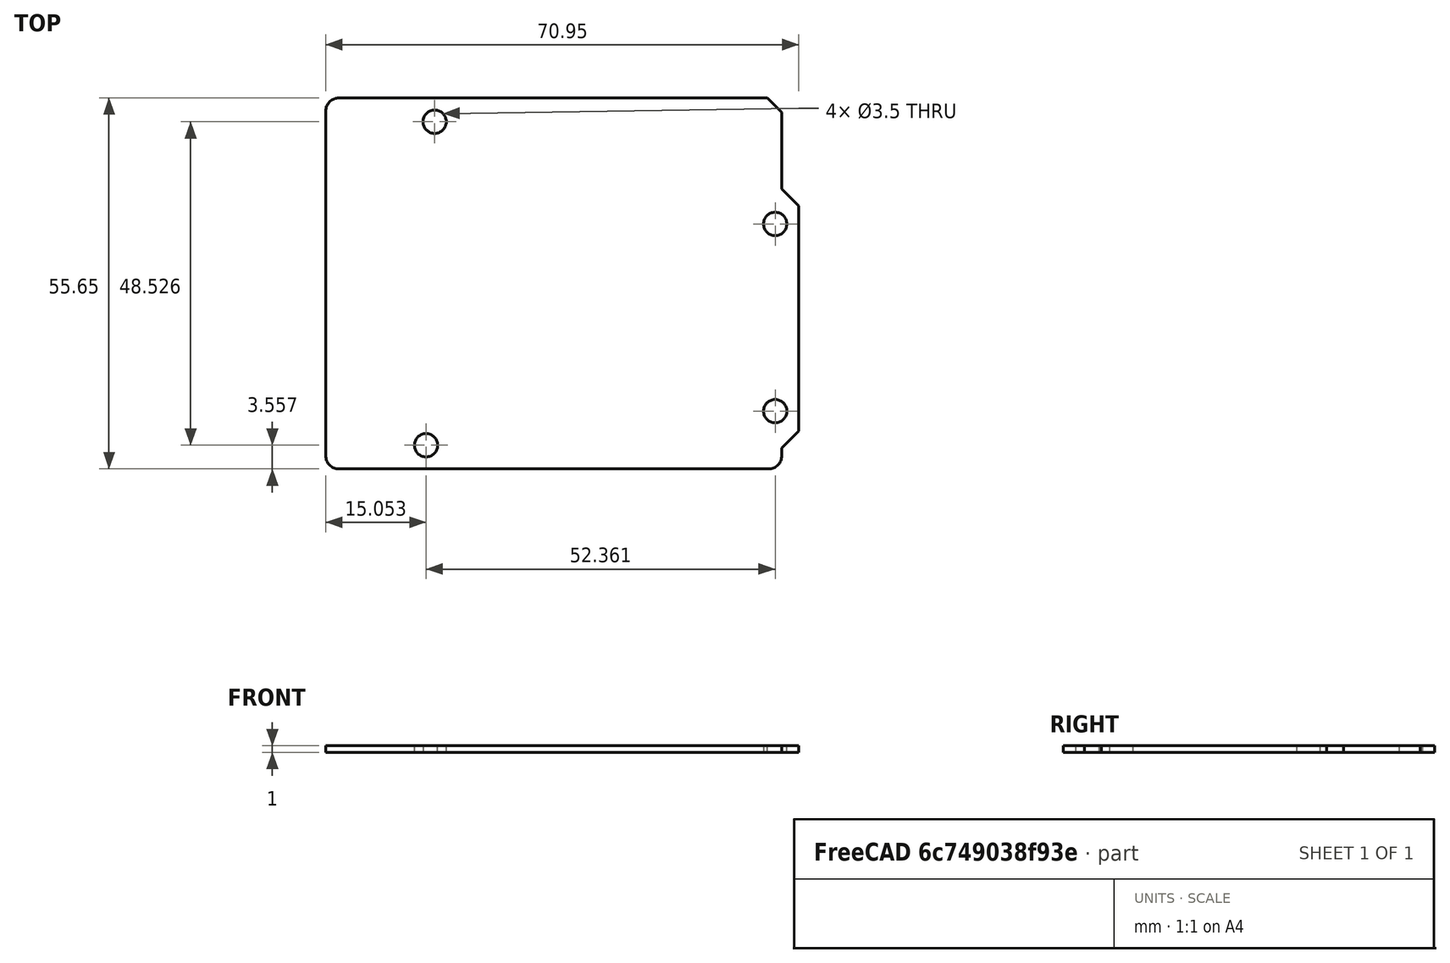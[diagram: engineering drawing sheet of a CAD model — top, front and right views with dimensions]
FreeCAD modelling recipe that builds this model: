
FCSTD DOCUMENT  (FreeCAD 0.19R)
Label: CASE-ARDUINO-CNC
License: Creative Commons Attribution-NonCommercial-ShareAlike
LicenseURL: http://creativecommons.org/licenses/by-nc-sa/4.0/
objects: Part::Feature×1, Sketcher::SketchObject×1, Part::Extrusion×1
note: 3 computed .brp shape members not serialized (recipe doc carries the construction recipe); baked Part::Feature solids carry a one-line shape summary decoded from their .brp

FEATURE [Part::Feature] ARDUINO_3D_SCALED
  Placement = pos=(-1,-1,0) rot=(0,0,1;0rad)
  shape: bbox 75.35 x 53.65 x 13.2 mm, 104 faces, 0 solids (baked)
FEATURE [Sketcher::SketchObject] Sketch
  ExternalGeometry = -> [ARDUINO_3D_SCALED]
  sketch-geometry (25):
    g0: LineSegment StartX=65.2642 StartY=54.65 StartZ=0 EndX=67.4 EndY=52.5142 EndZ=0
    g1: LineSegment StartX=67.4 StartY=52.5142 StartZ=0 EndX=67.4 EndY=41.0142 EndZ=0
    g2: LineSegment StartX=67.4 StartY=41.0142 StartZ=0 EndX=69.95 EndY=38.4642 EndZ=0
    g3: LineSegment StartX=69.95 StartY=38.4642 StartZ=0 EndX=69.95 EndY=4.68579 EndZ=0
    g4: LineSegment StartX=69.95 StartY=4.68579 StartZ=0 EndX=67.4 EndY=2.13579 EndZ=0
    g5: LineSegment StartX=67.4 StartY=2.13579 StartZ=0 EndX=67.4 EndY=1 EndZ=0
    g6: LineSegment StartX=65.4 StartY=-1 StartZ=0 EndX=1 EndY=-1 EndZ=0
    g7: LineSegment StartX=-1 StartY=1 StartZ=0 EndX=-1 EndY=52.65 EndZ=0
    g8: LineSegment StartX=1 StartY=54.65 StartZ=0 EndX=65.2642 EndY=54.65 EndZ=0
    g9: ArcOfCircle CenterX=1 CenterY=1 CenterZ=0 NormalX=0 NormalY=0 NormalZ=1 AngleXU=0 Radius=2 StartAngle=3.14159 EndAngle=4.71239
    g10: ArcOfCircle CenterX=65.4 CenterY=1 CenterZ=0 NormalX=0 NormalY=0 NormalZ=1 AngleXU=0 Radius=2 StartAngle=4.71239 EndAngle=6.28319
    g11: ArcOfCircle CenterX=1 CenterY=52.65 CenterZ=0 NormalX=0 NormalY=0 NormalZ=1 AngleXU=0 Radius=2 StartAngle=1.5708 EndAngle=3.14159
    g12: LineSegment [constr] StartX=65.625 StartY=52.875 StartZ=0 EndX=66.3321 EndY=53.5821 EndZ=0
    g13: LineSegment [constr] StartX=67.675 StartY=39.325 StartZ=0 EndX=68.3821 EndY=40.0321 EndZ=0
    g14: LineSegment [constr] StartX=67.675 StartY=3.825 StartZ=0 EndX=68.3821 EndY=3.11789 EndZ=0
    g15: LineSegment [constr] StartX=68.95 StartY=21.575 StartZ=0 EndX=69.95 EndY=21.575 EndZ=0
    g16: LineSegment [constr] StartX=33.2 StartY=0 StartZ=0 EndX=33.2 EndY=-1 EndZ=0
    g17: LineSegment [constr] StartX=32.925 StartY=53.65 StartZ=0 EndX=32.925 EndY=54.65 EndZ=0
    g18: LineSegment [constr] StartX=0 StartY=26.825 StartZ=0 EndX=-1 EndY=26.825 EndZ=0
    g19: LineSegment [constr] StartX=66.4 StartY=46.35 StartZ=0 EndX=67.4 EndY=46.35 EndZ=0
    g20: LineSegment [constr] StartX=66.4 StartY=1.775 StartZ=0 EndX=67.4 EndY=1.775 EndZ=0
    g21: Circle CenterX=14.0525 CenterY=2.55698 CenterZ=0 NormalX=0 NormalY=0 NormalZ=1 AngleXU=0 Radius=1.75
    g22: Circle CenterX=66.4139 CenterY=7.6684 CenterZ=0 NormalX=0 NormalY=0 NormalZ=1 AngleXU=0 Radius=1.75
    g23: Circle CenterX=66.41 CenterY=35.7498 CenterZ=0 NormalX=0 NormalY=0 NormalZ=1 AngleXU=0 Radius=1.75
    g24: Circle CenterX=15.3341 CenterY=51.0829 CenterZ=0 NormalX=0 NormalY=0 NormalZ=1 AngleXU=0 Radius=1.75
  constraints (65):
    c: Coincident(g0,g1)
    c: Vertical(g1)
    c: Coincident(g1,g2)
    c: Coincident(g2,g3)
    c: Vertical(g3)
    c: Coincident(g3,g4)
    c: Coincident(g4,g5)
    c: Vertical(g5)
    c: Horizontal(g6)
    c: Vertical(g7)
    c: Coincident(g8,g0)
    c: Horizontal(g8)
    c: Tangent(g6,g9) = 1.5708
    c: Tangent(g7,g9) = 1.5708
    c: Tangent(g5,g10) = 1.5708
    c: Tangent(g6,g10) = 1.5708
    c: Tangent(g8,g11) = 1.5708
    c: Tangent(g7,g11) = 1.5708
    c: Coincident(g11,g-14)
    c: Coincident(g10,g-10)
    c: Coincident(g9,g-12)
    c: Parallel(g-4,g0)
    c: Parallel(g-6,g2)
    c: Parallel(g4,g-8)
    c: PointOnObject(g12,g0)
    c: PointOnObject(g13,g2)
    c: PointOnObject(g14,g4)
    c: PointOnObject(g15,g3)
    c: Vertical(g16)
    c: PointOnObject(g17,g8)
    c: Vertical(g17)
    c: Horizontal(g15)
    c: Horizontal(g18)
    c: PointOnObject(g19,g1)
    c: Horizontal(g19)
    c: Symmetric(g-7,g-7,g15)
    c: Symmetric(g-8,g-8,g14)
    c: Symmetric(g-9,g-9,g20)
    c: Symmetric(g-11,g-11,g16)
    c: Symmetric(g-13,g-13,g18)
    c: Symmetric(g-3,g-3,g17)
    c: Symmetric(g-4,g-4,g12)
    c: Symmetric(g-5,g-5,g19)
    c: Symmetric(g-6,g-6,g13)
    c: Perpendicular(g-6,g13)
    c: Perpendicular(g-4,g12)
    c: Perpendicular(g-8,g14)
    c: Equal(g14,g20)
    c: Equal(g20,g16)
    c: Equal(g16,g18)
    c: Equal(g18,g17)
    c: Equal(g17,g12)
    c: Equal(g12,g19)
    c: Equal(g19,g13)
    c: Equal(g13,g15)
    c: Horizontal(g20)
    c: DistanceY(g17,g17) = 1
    c: Coincident(g21,g-18)
    c: Coincident(g22,g-17)
    c: Coincident(g23,g-16)
    c: Coincident(g24,g-15)
    c: Diameter(g21) = 3.5
    c: Equal(g21,g22)
    c: Equal(g21,g23)
    c: Equal(g21,g24)
FEATURE [Part::Extrusion] Extrude
  Base = -> Sketch
  Dir = (0,0,1)
  DirMode = 2
  FaceMakerClass = Part::FaceMakerBullseye
  LengthFwd = 1
  LengthRev = 0
  Solid = true
  Symmetric = false
